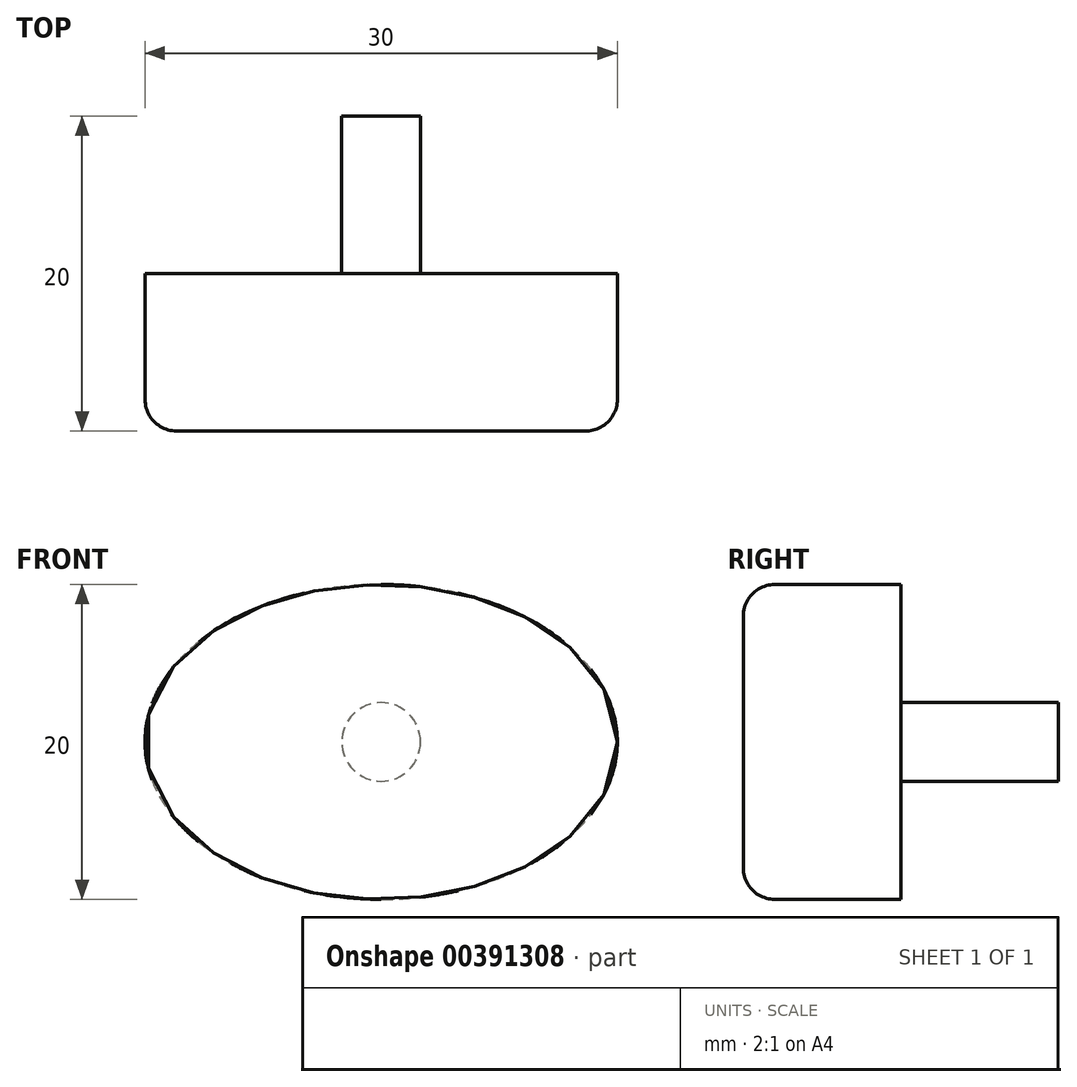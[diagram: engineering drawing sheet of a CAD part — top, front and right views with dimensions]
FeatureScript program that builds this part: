
annotation { "Feature Type Name" : "Feature", "Feature Type Description" : "" }
export const myFeature = defineFeature(function(context is Context, id is Id, definition is map)
    precondition{}
    {
        {
            var Q0;
            Q0=qCreatedBy(makeId("Front.planeOp"),FACE);
            var sketch = newSketch(context, id + "F0", { "sketchPlane" : qUnion([Q0])});
            skEllipse(sketch, "E0", {"center": v(0, 0) * mm, "majorRadius": 15 * mm, "minorRadius": 10 * mm, "majorAxis": v(1, 0)});
            skSolve(sketch);
        }
        {
            var Q0;
            Q0=makeQuery(id+"F0.imprint","IMPRINT",FACE,{"disambiguationData":[TD([[makeQuery(id+"F0.imprint","IMPRINT",EDGE,{"derivedFrom":sQuery(id+"F0.wireOp",EDGE,"E0")}),1.0]])]});
            extrude(context, id + "F1", {"entities" : qUnion([Q0]), "depth" : 10 * mm});
        }
        {
            var Q0;
            Q0=makeQuery(id+"F1.opExtrude","CAP_EDGE",EDGE,{"disambiguationData":[OSD([sQuery(id+"F0.wireOp",EDGE,"E0")])],"isStart":false});
            fillet(context, id + "F2", {"entities" : qUnion([Q0]), "radius" : 2 * mm, "tangentPropagation" : true, "allowEdgeOverflow" : false});
        }
        {
            var Q0;
            Q0=makeQuery(id+"F1.opExtrude","CAP_FACE",FACE,{"disambiguationData":[OSD([sQuery(id+"F0.wireOp",EDGE,"E0")])],"isStart":true});
            var sketch = newSketch(context, id + "F3", { "sketchPlane" : qUnion([Q0])});
            skCircle(sketch, "E1", {"center": v(0, 0) * mm, "radius": 2.5 * mm});
            skSolve(sketch);
        }
        {
            var Q0;
            Q0 = qSketchRegion(id + "F3", true);
            extrude(context, id + "F4", {"entities" : qUnion([Q0]), "operationType" : NewBodyOperationType.ADD, "depth" : 10 * mm});
        }
    });
